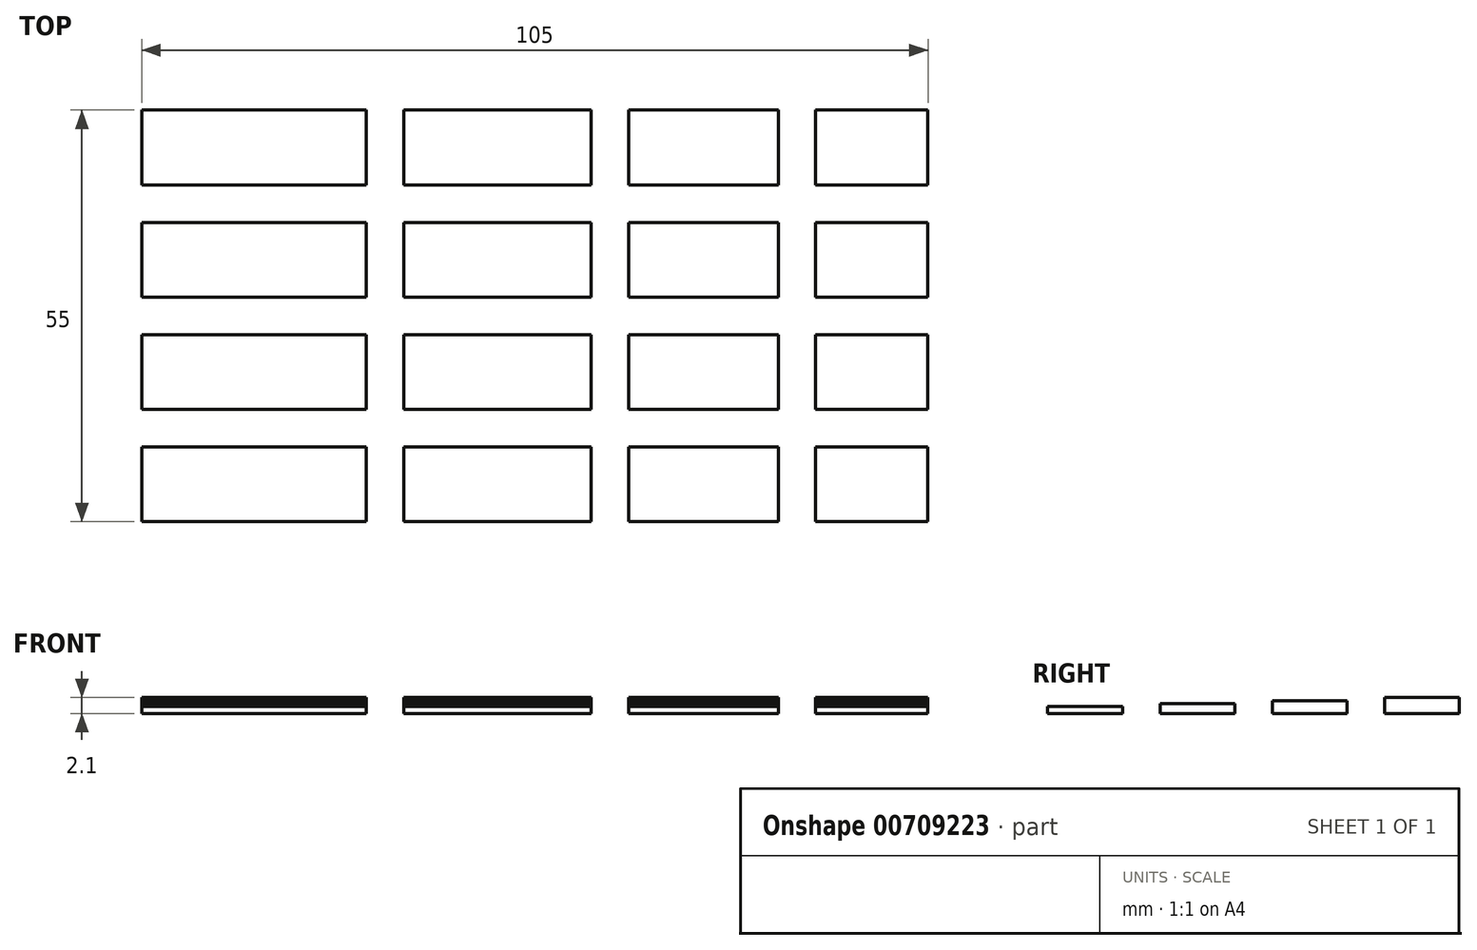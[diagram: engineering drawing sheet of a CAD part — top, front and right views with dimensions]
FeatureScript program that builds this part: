
annotation { "Feature Type Name" : "Feature", "Feature Type Description" : "" }
export const myFeature = defineFeature(function(context is Context, id is Id, definition is map)
    precondition{}
    {
        {
            var Q0;
            Q0=qCreatedBy(makeId("Top.planeOp"),FACE);
            var sketch = newSketch(context, id + "F0", { "sketchPlane" : qUnion([Q0])});
            skLineSegment(sketch, "E0.bottom", {"start": v(-44.9, 27.14) * mm, "end": v(-14.9, 27.14) * mm});
            skLineSegment(sketch, "E0.top", {"start": v(-44.9, 17.14) * mm, "end": v(-14.9, 17.14) * mm});
            skLineSegment(sketch, "E0.left", {"start": v(-44.9, 27.14) * mm, "end": v(-44.9, 17.14) * mm});
            skLineSegment(sketch, "E0.right", {"start": v(-14.9, 27.14) * mm, "end": v(-14.9, 17.14) * mm});
            skLineSegment(sketch, "E1.bottom", {"start": v(-9.9, 27.14) * mm, "end": v(15.1, 27.14) * mm});
            skLineSegment(sketch, "E1.top", {"start": v(-9.9, 17.14) * mm, "end": v(15.1, 17.14) * mm});
            skLineSegment(sketch, "E1.left", {"start": v(-9.9, 27.14) * mm, "end": v(-9.9, 17.14) * mm});
            skLineSegment(sketch, "E1.right", {"start": v(15.1, 27.14) * mm, "end": v(15.1, 17.14) * mm});
            skLineSegment(sketch, "E2.bottom", {"start": v(20.1, 27.14) * mm, "end": v(40.1, 27.14) * mm});
            skLineSegment(sketch, "E2.top", {"start": v(20.1, 17.14) * mm, "end": v(40.1, 17.14) * mm});
            skLineSegment(sketch, "E2.left", {"start": v(20.1, 27.14) * mm, "end": v(20.1, 17.14) * mm});
            skLineSegment(sketch, "E2.right", {"start": v(40.1, 27.14) * mm, "end": v(40.1, 17.14) * mm});
            skLineSegment(sketch, "E3.bottom", {"start": v(45.1, 27.14) * mm, "end": v(60.1, 27.14) * mm});
            skLineSegment(sketch, "E3.top", {"start": v(45.1, 17.14) * mm, "end": v(60.1, 17.14) * mm});
            skLineSegment(sketch, "E3.left", {"start": v(45.1, 27.14) * mm, "end": v(45.1, 17.14) * mm});
            skLineSegment(sketch, "E3.right", {"start": v(60.1, 27.14) * mm, "end": v(60.1, 17.14) * mm});
            skLineSegment(sketch, "E4.0.1.0", {"start": v(20.1, 2.14) * mm, "end": v(40.1, 2.14) * mm});
            skLineSegment(sketch, "E4.0.1.1", {"start": v(20.1, 12.14) * mm, "end": v(40.1, 12.14) * mm});
            skLineSegment(sketch, "E4.0.1.2", {"start": v(15.1, 12.14) * mm, "end": v(15.1, 2.14) * mm});
            skLineSegment(sketch, "E4.0.1.3", {"start": v(-44.9, 12.14) * mm, "end": v(-14.9, 12.14) * mm});
            skLineSegment(sketch, "E4.0.1.4", {"start": v(-9.9, 12.14) * mm, "end": v(-9.9, 2.14) * mm});
            skLineSegment(sketch, "E4.0.1.5", {"start": v(20.1, 12.14) * mm, "end": v(20.1, 2.14) * mm});
            skLineSegment(sketch, "E4.0.1.6", {"start": v(40.1, 12.14) * mm, "end": v(40.1, 2.14) * mm});
            skLineSegment(sketch, "E4.0.1.7", {"start": v(45.1, 12.14) * mm, "end": v(60.1, 12.14) * mm});
            skLineSegment(sketch, "E4.0.1.8", {"start": v(-44.9, 2.14) * mm, "end": v(-14.9, 2.14) * mm});
            skLineSegment(sketch, "E4.0.1.9", {"start": v(-9.9, 2.14) * mm, "end": v(15.1, 2.14) * mm});
            skLineSegment(sketch, "E4.0.1.10", {"start": v(-9.9, 12.14) * mm, "end": v(15.1, 12.14) * mm});
            skLineSegment(sketch, "E4.0.1.11", {"start": v(-14.9, 12.14) * mm, "end": v(-14.9, 2.14) * mm});
            skLineSegment(sketch, "E4.0.1.12", {"start": v(-44.9, 12.14) * mm, "end": v(-44.9, 2.14) * mm});
            skLineSegment(sketch, "E4.0.1.13", {"start": v(60.1, 12.14) * mm, "end": v(60.1, 2.14) * mm});
            skLineSegment(sketch, "E4.0.1.14", {"start": v(45.1, 12.14) * mm, "end": v(45.1, 2.14) * mm});
            skLineSegment(sketch, "E4.0.1.15", {"start": v(45.1, 2.14) * mm, "end": v(60.1, 2.14) * mm});
            skLineSegment(sketch, "E4.0.2.0", {"start": v(20.1, -12.86) * mm, "end": v(40.1, -12.86) * mm});
            skLineSegment(sketch, "E4.0.2.1", {"start": v(20.1, -2.86) * mm, "end": v(40.1, -2.86) * mm});
            skLineSegment(sketch, "E4.0.2.2", {"start": v(15.1, -2.86) * mm, "end": v(15.1, -12.86) * mm});
            skLineSegment(sketch, "E4.0.2.3", {"start": v(-44.9, -2.86) * mm, "end": v(-14.9, -2.86) * mm});
            skLineSegment(sketch, "E4.0.2.4", {"start": v(-9.9, -2.86) * mm, "end": v(-9.9, -12.86) * mm});
            skLineSegment(sketch, "E4.0.2.5", {"start": v(20.1, -2.86) * mm, "end": v(20.1, -12.86) * mm});
            skLineSegment(sketch, "E4.0.2.6", {"start": v(40.1, -2.86) * mm, "end": v(40.1, -12.86) * mm});
            skLineSegment(sketch, "E4.0.2.7", {"start": v(45.1, -2.86) * mm, "end": v(60.1, -2.86) * mm});
            skLineSegment(sketch, "E4.0.2.8", {"start": v(-44.9, -12.86) * mm, "end": v(-14.9, -12.86) * mm});
            skLineSegment(sketch, "E4.0.2.9", {"start": v(-9.9, -12.86) * mm, "end": v(15.1, -12.86) * mm});
            skLineSegment(sketch, "E4.0.2.10", {"start": v(-9.9, -2.86) * mm, "end": v(15.1, -2.86) * mm});
            skLineSegment(sketch, "E4.0.2.11", {"start": v(-14.9, -2.86) * mm, "end": v(-14.9, -12.86) * mm});
            skLineSegment(sketch, "E4.0.2.12", {"start": v(-44.9, -2.86) * mm, "end": v(-44.9, -12.86) * mm});
            skLineSegment(sketch, "E4.0.2.13", {"start": v(60.1, -2.86) * mm, "end": v(60.1, -12.86) * mm});
            skLineSegment(sketch, "E4.0.2.14", {"start": v(45.1, -2.86) * mm, "end": v(45.1, -12.86) * mm});
            skLineSegment(sketch, "E4.0.2.15", {"start": v(45.1, -12.86) * mm, "end": v(60.1, -12.86) * mm});
            skLineSegment(sketch, "E4.0.3.0", {"start": v(20.1, -27.86) * mm, "end": v(40.1, -27.86) * mm});
            skLineSegment(sketch, "E4.0.3.1", {"start": v(20.1, -17.86) * mm, "end": v(40.1, -17.86) * mm});
            skLineSegment(sketch, "E4.0.3.2", {"start": v(15.1, -17.86) * mm, "end": v(15.1, -27.86) * mm});
            skLineSegment(sketch, "E4.0.3.3", {"start": v(-44.9, -17.86) * mm, "end": v(-14.9, -17.86) * mm});
            skLineSegment(sketch, "E4.0.3.4", {"start": v(-9.9, -17.86) * mm, "end": v(-9.9, -27.86) * mm});
            skLineSegment(sketch, "E4.0.3.5", {"start": v(20.1, -17.86) * mm, "end": v(20.1, -27.86) * mm});
            skLineSegment(sketch, "E4.0.3.6", {"start": v(40.1, -17.86) * mm, "end": v(40.1, -27.86) * mm});
            skLineSegment(sketch, "E4.0.3.7", {"start": v(45.1, -17.86) * mm, "end": v(60.1, -17.86) * mm});
            skLineSegment(sketch, "E4.0.3.8", {"start": v(-44.9, -27.86) * mm, "end": v(-14.9, -27.86) * mm});
            skLineSegment(sketch, "E4.0.3.9", {"start": v(-9.9, -27.86) * mm, "end": v(15.1, -27.86) * mm});
            skLineSegment(sketch, "E4.0.3.10", {"start": v(-9.9, -17.86) * mm, "end": v(15.1, -17.86) * mm});
            skLineSegment(sketch, "E4.0.3.11", {"start": v(-14.9, -17.86) * mm, "end": v(-14.9, -27.86) * mm});
            skLineSegment(sketch, "E4.0.3.12", {"start": v(-44.9, -17.86) * mm, "end": v(-44.9, -27.86) * mm});
            skLineSegment(sketch, "E4.0.3.13", {"start": v(60.1, -17.86) * mm, "end": v(60.1, -27.86) * mm});
            skLineSegment(sketch, "E4.0.3.14", {"start": v(45.1, -17.86) * mm, "end": v(45.1, -27.86) * mm});
            skLineSegment(sketch, "E4.0.3.15", {"start": v(45.1, -27.86) * mm, "end": v(60.1, -27.86) * mm});
            skLineSegment(sketch, "E4.direction1", {"start": v(-44.9, 17.14) * mm, "end": v(-19.9, 17.14) * mm, "construction": true});
            skLineSegment(sketch, "E4.direction2", {"start": v(-44.9, 17.14) * mm, "end": v(-44.9, 2.14) * mm, "construction": true});
            skSolve(sketch);
        }
        {
            var Q0;
            Q0=makeQuery(id+"F0.imprint","IMPRINT",FACE,{"disambiguationData":[TD([[makeQuery(id+"F0.imprint","IMPRINT",EDGE,{"derivedFrom":sQuery(id+"F0.wireOp",EDGE,"E0.bottom")}),-1.0]])]});
            var Q1;
            Q1=makeQuery(id+"F0.imprint","IMPRINT",FACE,{"disambiguationData":[TD([[makeQuery(id+"F0.imprint","IMPRINT",EDGE,{"derivedFrom":sQuery(id+"F0.wireOp",EDGE,"E1.bottom")}),-1.0]])]});
            var Q2;
            Q2=makeQuery(id+"F0.imprint","IMPRINT",FACE,{"disambiguationData":[TD([[makeQuery(id+"F0.imprint","IMPRINT",EDGE,{"derivedFrom":sQuery(id+"F0.wireOp",EDGE,"E2.bottom")}),-1.0]])]});
            var Q3;
            Q3=makeQuery(id+"F0.imprint","IMPRINT",FACE,{"disambiguationData":[TD([[makeQuery(id+"F0.imprint","IMPRINT",EDGE,{"derivedFrom":sQuery(id+"F0.wireOp",EDGE,"E3.bottom")}),-1.0]])]});
            extrude(context, id + "F1", {"entities" : qUnion([Q0, Q1, Q2, Q3]), "depth" : 2.1 * mm, "offsetDistance" : 25 * mm});
        }
        {
            var Q0;
            Q0=makeQuery(id+"F0.imprint","IMPRINT",FACE,{"disambiguationData":[TD([[makeQuery(id+"F0.imprint","IMPRINT",EDGE,{"derivedFrom":sQuery(id+"F0.wireOp",EDGE,"E4.0.1.3")}),-1.0]])]});
            var Q1;
            Q1=makeQuery(id+"F0.imprint","IMPRINT",FACE,{"disambiguationData":[TD([[makeQuery(id+"F0.imprint","IMPRINT",EDGE,{"derivedFrom":sQuery(id+"F0.wireOp",EDGE,"E4.0.1.2")}),-1.0]])]});
            var Q2;
            Q2=makeQuery(id+"F0.imprint","IMPRINT",FACE,{"disambiguationData":[TD([[makeQuery(id+"F0.imprint","IMPRINT",EDGE,{"derivedFrom":sQuery(id+"F0.wireOp",EDGE,"E4.0.1.0")}),1.0]])]});
            var Q3;
            Q3=makeQuery(id+"F0.imprint","IMPRINT",FACE,{"disambiguationData":[TD([[makeQuery(id+"F0.imprint","IMPRINT",EDGE,{"derivedFrom":sQuery(id+"F0.wireOp",EDGE,"E4.0.1.7")}),-1.0]])]});
            extrude(context, id + "F2", {"entities" : qUnion([Q0, Q1, Q2, Q3]), "depth" : 1.7 * mm, "offsetDistance" : 25 * mm});
        }
        {
            var Q0;
            Q0=makeQuery(id+"F0.imprint","IMPRINT",FACE,{"disambiguationData":[TD([[makeQuery(id+"F0.imprint","IMPRINT",EDGE,{"derivedFrom":sQuery(id+"F0.wireOp",EDGE,"E4.0.2.3")}),-1.0]])]});
            var Q1;
            Q1=makeQuery(id+"F0.imprint","IMPRINT",FACE,{"disambiguationData":[TD([[makeQuery(id+"F0.imprint","IMPRINT",EDGE,{"derivedFrom":sQuery(id+"F0.wireOp",EDGE,"E4.0.2.2")}),-1.0]])]});
            var Q2;
            Q2=makeQuery(id+"F0.imprint","IMPRINT",FACE,{"disambiguationData":[TD([[makeQuery(id+"F0.imprint","IMPRINT",EDGE,{"derivedFrom":sQuery(id+"F0.wireOp",EDGE,"E4.0.2.0")}),1.0]])]});
            var Q3;
            Q3=makeQuery(id+"F0.imprint","IMPRINT",FACE,{"disambiguationData":[TD([[makeQuery(id+"F0.imprint","IMPRINT",EDGE,{"derivedFrom":sQuery(id+"F0.wireOp",EDGE,"E4.0.2.7")}),-1.0]])]});
            extrude(context, id + "F3", {"entities" : qUnion([Q0, Q1, Q2, Q3]), "depth" : 1.3 * mm, "offsetDistance" : 25 * mm});
        }
        {
            var Q0;
            Q0=makeQuery(id+"F0.imprint","IMPRINT",FACE,{"disambiguationData":[TD([[makeQuery(id+"F0.imprint","IMPRINT",EDGE,{"derivedFrom":sQuery(id+"F0.wireOp",EDGE,"E4.0.3.3")}),-1.0]])]});
            var Q1;
            Q1=makeQuery(id+"F0.imprint","IMPRINT",FACE,{"disambiguationData":[TD([[makeQuery(id+"F0.imprint","IMPRINT",EDGE,{"derivedFrom":sQuery(id+"F0.wireOp",EDGE,"E4.0.3.2")}),-1.0]])]});
            var Q2;
            Q2=makeQuery(id+"F0.imprint","IMPRINT",FACE,{"disambiguationData":[TD([[makeQuery(id+"F0.imprint","IMPRINT",EDGE,{"derivedFrom":sQuery(id+"F0.wireOp",EDGE,"E4.0.3.0")}),1.0]])]});
            var Q3;
            Q3=makeQuery(id+"F0.imprint","IMPRINT",FACE,{"disambiguationData":[TD([[makeQuery(id+"F0.imprint","IMPRINT",EDGE,{"derivedFrom":sQuery(id+"F0.wireOp",EDGE,"E4.0.3.7")}),-1.0]])]});
            extrude(context, id + "F4", {"entities" : qUnion([Q0, Q1, Q2, Q3]), "depth" : 0.9 * mm, "offsetDistance" : 25 * mm});
        }
    });
